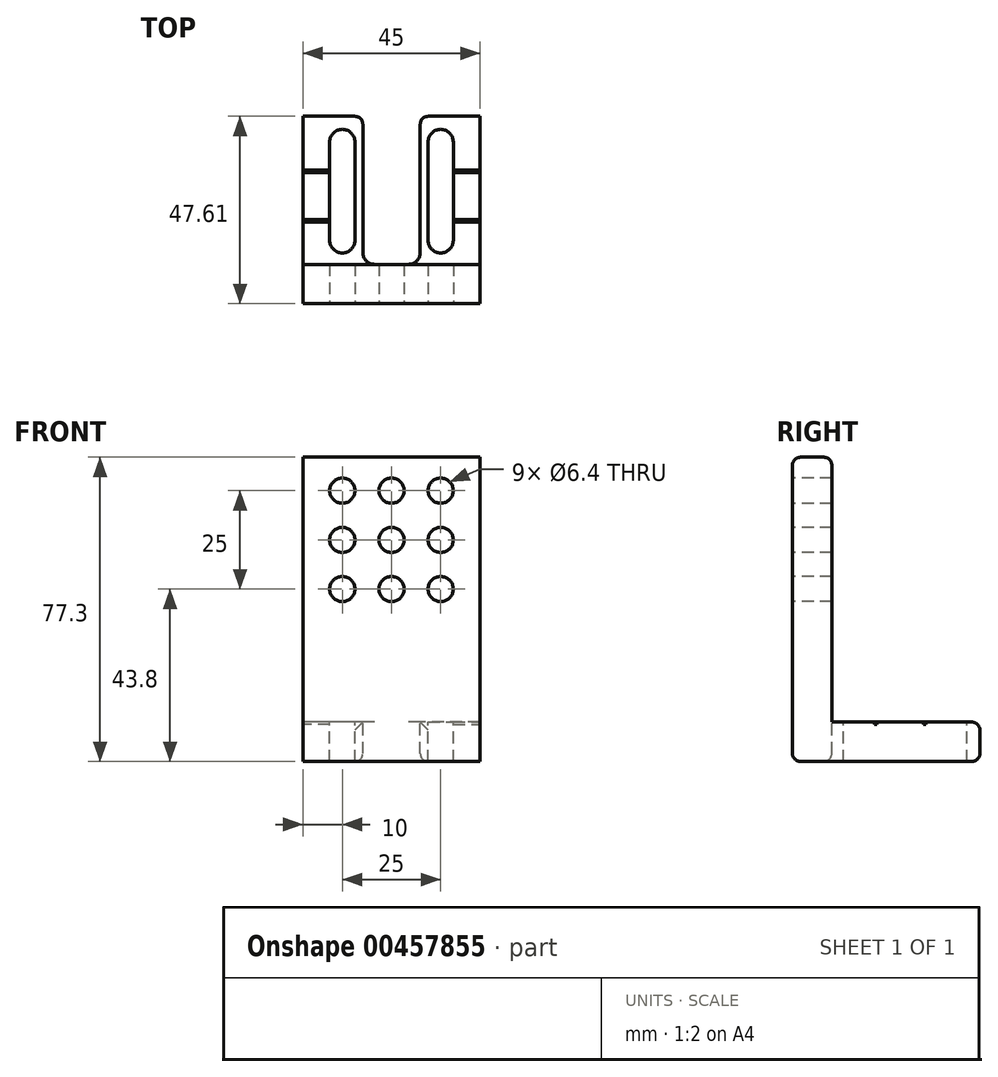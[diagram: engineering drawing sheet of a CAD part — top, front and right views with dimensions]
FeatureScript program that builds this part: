
annotation { "Feature Type Name" : "Feature", "Feature Type Description" : "" }
export const myFeature = defineFeature(function(context is Context, id is Id, definition is map)
    precondition{}
    {
        {
            var Q0;
            Q0=qCreatedBy(makeId("Right.planeOp"),FACE);
            var sketch = newSketch(context, id + "F0", { "sketchPlane" : qUnion([Q0])});
            skLineSegment(sketch, "E0", {"start": v(0, 0) * mm, "end": v(0, 67.3) * mm});
            skLineSegment(sketch, "E1", {"start": v(0, 67.3) * mm, "end": v(-10, 67.3) * mm});
            skLineSegment(sketch, "E2", {"start": v(-10, 67.3) * mm, "end": v(-10, -10) * mm});
            skLineSegment(sketch, "E3", {"start": v(-10, -10) * mm, "end": v(37.61, -10) * mm});
            skLineSegment(sketch, "E4", {"start": v(37.61, -10) * mm, "end": v(37.61, 0) * mm});
            skLineSegment(sketch, "E5", {"start": v(37.61, 0) * mm, "end": v(0, 0) * mm});
            skLineSegment(sketch, "E6", {"start": v(-10, 46.3) * mm, "end": v(0, 46.3) * mm, "construction": true});
            skLineSegment(sketch, "E7", {"start": v(23.61, 0) * mm, "end": v(23.61, -10) * mm, "construction": true});
            skLineSegment(sketch, "E8", {"start": v(11.11, 0) * mm, "end": v(11.11, -10) * mm, "construction": true});
            skLineSegment(sketch, "E9", {"start": v(6, 0) * mm, "end": v(6, -10) * mm, "construction": true});
            skPoint(sketch, "E9.endSnap0", {"position": v(13.8, -10) * mm});
            skSolve(sketch);
        }
        {
            var Q0;
            Q0=makeQuery(id+"F0.imprint","IMPRINT",FACE,{"disambiguationData":[TD([[makeQuery(id+"F0.imprint","IMPRINT",EDGE,{"derivedFrom":sQuery(id+"F0.wireOp",EDGE,"E0")}),1.0]])]});
            extrude(context, id + "F1", {"entities" : qUnion([Q0]), "depth" : 45 * mm});
        }
        {
            var Q0;
            Q0=makeQuery(id+"F1.opExtrude","SWEPT_FACE",FACE,{"disambiguationData":[OSD([sQuery(id+"F0.wireOp",EDGE,"E5")])]});
            var sketch = newSketch(context, id + "F2", { "sketchPlane" : qUnion([Q0])});
            skLineSegment(sketch, "E10", {"start": v(22.5, 37.61) * mm, "end": v(22.5, 0) * mm, "construction": true});
            skPoint(sketch, "E11.0", {"position": v(0, 23.61) * mm});
            skPoint(sketch, "E12.0", {"position": v(0, 11.11) * mm});
            skCircle(sketch, "E13", {"center": v(10, 23.61) * mm, "radius": 3.2 * mm, "construction": true});
            skCircle(sketch, "E14", {"center": v(10, 11.11) * mm, "radius": 3.2 * mm, "construction": true});
            skCircle(sketch, "E15", {"center": v(35, 11.11) * mm, "radius": 3.2 * mm, "construction": true});
            skCircle(sketch, "E16", {"center": v(35, 23.61) * mm, "radius": 3.2 * mm, "construction": true});
            skArc(sketch, "E17", {"start": v(13.2, 31.11) * mm, "mid": v(10, 34.31) * mm, "end": v(6.8, 31.11) * mm});
            skArc(sketch, "E18", {"start": v(38.2, 31.11) * mm, "mid": v(35, 34.31) * mm, "end": v(31.8, 31.11) * mm});
            skArc(sketch, "E19", {"start": v(6.8, 6.11) * mm, "mid": v(10, 2.91) * mm, "end": v(13.2, 6.11) * mm});
            skArc(sketch, "E20", {"start": v(31.8, 6.11) * mm, "mid": v(35, 2.91) * mm, "end": v(38.2, 6.11) * mm});
            skLineSegment(sketch, "E21", {"start": v(6.8, 31.11) * mm, "end": v(6.8, 6.11) * mm});
            skLineSegment(sketch, "E22", {"start": v(13.2, 31.11) * mm, "end": v(13.2, 6.11) * mm});
            skLineSegment(sketch, "E23", {"start": v(31.8, 31.11) * mm, "end": v(31.8, 6.11) * mm});
            skLineSegment(sketch, "E24", {"start": v(38.2, 6.11) * mm, "end": v(38.2, 31.11) * mm});
            skLineSegment(sketch, "E25.bottom", {"start": v(15.2, 37.61) * mm, "end": v(29.8, 37.61) * mm});
            skLineSegment(sketch, "E25.top", {"start": v(15.2, 0) * mm, "end": v(29.8, 0) * mm});
            skLineSegment(sketch, "E25.left", {"start": v(15.2, 37.61) * mm, "end": v(15.2, 0) * mm});
            skLineSegment(sketch, "E25.right", {"start": v(29.8, 37.61) * mm, "end": v(29.8, 0) * mm});
            skLineSegment(sketch, "E26.bottom", {"start": v(6.8, 10.81) * mm, "end": v(0, 10.81) * mm});
            skLineSegment(sketch, "E26.top", {"start": v(6.8, 11.41) * mm, "end": v(0, 11.41) * mm});
            skLineSegment(sketch, "E26.left", {"start": v(6.8, 10.81) * mm, "end": v(6.8, 11.41) * mm});
            skLineSegment(sketch, "E26.right", {"start": v(0, 10.81) * mm, "end": v(0, 11.41) * mm});
            skLineSegment(sketch, "E27.bottom", {"start": v(6.8, 23.31) * mm, "end": v(0, 23.31) * mm});
            skLineSegment(sketch, "E27.top", {"start": v(6.8, 23.91) * mm, "end": v(0, 23.91) * mm});
            skLineSegment(sketch, "E27.left", {"start": v(6.8, 23.31) * mm, "end": v(6.8, 23.91) * mm});
            skLineSegment(sketch, "E27.right", {"start": v(0, 23.31) * mm, "end": v(0, 23.91) * mm});
            skLineSegment(sketch, "E28.bottom", {"start": v(38.2, 10.81) * mm, "end": v(45, 10.81) * mm});
            skLineSegment(sketch, "E28.top", {"start": v(38.2, 11.41) * mm, "end": v(45, 11.41) * mm});
            skLineSegment(sketch, "E28.left", {"start": v(38.2, 10.81) * mm, "end": v(38.2, 11.41) * mm});
            skLineSegment(sketch, "E28.right", {"start": v(45, 10.81) * mm, "end": v(45, 11.41) * mm});
            skLineSegment(sketch, "E29.bottom", {"start": v(38.2, 23.31) * mm, "end": v(45, 23.31) * mm});
            skLineSegment(sketch, "E29.top", {"start": v(38.2, 23.91) * mm, "end": v(45, 23.91) * mm});
            skLineSegment(sketch, "E29.left", {"start": v(38.2, 23.31) * mm, "end": v(38.2, 23.91) * mm});
            skLineSegment(sketch, "E29.right", {"start": v(45, 23.31) * mm, "end": v(45, 23.91) * mm});
            skSolve(sketch);
        }
        {
            var Q0;
            Q0=makeQuery(id+"F2.imprint","IMPRINT",FACE,{"disambiguationData":[TD([[makeQuery(id+"F2.imprint","IMPRINT",EDGE,{"derivedFrom":sQuery(id+"F2.wireOp",EDGE,"E17")}),1.0]])]});
            var Q1;
            Q1=makeQuery(id+"F2.imprint","IMPRINT",FACE,{"disambiguationData":[TD([[makeQuery(id+"F2.imprint","IMPRINT",EDGE,{"derivedFrom":sQuery(id+"F2.wireOp",EDGE,"o95GAQiW-py6V-pouL-C4bO-UlPNCyXJZhJI")}),1.0]])]});
            var Q2;
            Q2=makeQuery(id+"F2.imprint","IMPRINT",FACE,{"disambiguationData":[TD([[makeQuery(id+"F2.imprint","IMPRINT",EDGE,{"derivedFrom":sQuery(id+"F2.wireOp",EDGE,"E18")}),1.0]])]});
            extrude(context, id + "F3", {"entities" : qUnion([Q0, Q1, Q2]), "operationType" : NewBodyOperationType.REMOVE, "oppositeDirection" : true, "depth" : 10 * mm});
        }
        {
            var Q0;
            Q0=makeQuery(id+"F1.opExtrude","SWEPT_EDGE",EDGE,{"disambiguationData":[OSD([sQuery(id+"F0.wireOp",EDGE,"E3"),sQuery(id+"F0.wireOp",EDGE,"E4")])]});
            var Q1;
            Q1=makeQuery(id+"F1.opExtrude","SWEPT_EDGE",EDGE,{"disambiguationData":[OSD([sQuery(id+"F0.wireOp",EDGE,"E2"),sQuery(id+"F0.wireOp",EDGE,"E3")])]});
            var Q2;
            Q2=makeQuery(id+"F1.opExtrude","SWEPT_EDGE",EDGE,{"disambiguationData":[OSD([sQuery(id+"F0.wireOp",EDGE,"E0"),sQuery(id+"F0.wireOp",EDGE,"E1")])]});
            var Q3;
            Q3=makeQuery(id+"F1.opExtrude","SWEPT_EDGE",EDGE,{"disambiguationData":[OSD([sQuery(id+"F0.wireOp",EDGE,"E1"),sQuery(id+"F0.wireOp",EDGE,"E2")])]});
            fillet(context, id + "F4", {"entities" : qUnion([Q0, Q1, Q2, Q3]), "radius" : 2 * mm, "tangentPropagation" : true, "allowEdgeOverflow" : false});
        }
        {
            var Q0;
            Q0=makeQuery(id+"F1.opExtrude","SWEPT_FACE",FACE,{"disambiguationData":[OSD([sQuery(id+"F0.wireOp",EDGE,"E2")])]});
            var sketch = newSketch(context, id + "F5", { "sketchPlane" : qUnion([Q0])});
            skPoint(sketch, "E30.0", {"position": v(0, 46.3) * mm});
            skCircle(sketch, "E31", {"center": v(22.5, 46.3) * mm, "radius": 3.2 * mm});
            skPoint(sketch, "E31.centerSnap0", {"position": v(22.5, 65.3) * mm});
            skCircle(sketch, "E32", {"center": v(22.5, 58.8) * mm, "radius": 3.2 * mm});
            skCircle(sketch, "E33", {"center": v(22.5, 33.8) * mm, "radius": 3.2 * mm});
            skCircle(sketch, "E34", {"center": v(35, 46.3) * mm, "radius": 3.2 * mm});
            skCircle(sketch, "E35", {"center": v(35, 58.8) * mm, "radius": 3.2 * mm});
            skCircle(sketch, "E36", {"center": v(35, 33.8) * mm, "radius": 3.2 * mm});
            skCircle(sketch, "E37", {"center": v(10, 58.8) * mm, "radius": 3.2 * mm});
            skCircle(sketch, "E38", {"center": v(10, 46.3) * mm, "radius": 3.2 * mm});
            skCircle(sketch, "E39", {"center": v(10, 33.8) * mm, "radius": 3.2 * mm});
            skSolve(sketch);
        }
        {
            var Q0;
            Q0=makeQuery(id+"F5.imprint","IMPRINT",FACE,{"disambiguationData":[TD([[makeQuery(id+"F5.imprint","IMPRINT",EDGE,{"derivedFrom":sQuery(id+"F5.wireOp",EDGE,"E37")}),1.0]])]});
            var Q1;
            Q1=makeQuery(id+"F5.imprint","IMPRINT",FACE,{"disambiguationData":[TD([[makeQuery(id+"F5.imprint","IMPRINT",EDGE,{"derivedFrom":sQuery(id+"F5.wireOp",EDGE,"E32")}),1.0]])]});
            var Q2;
            Q2=makeQuery(id+"F5.imprint","IMPRINT",FACE,{"disambiguationData":[TD([[makeQuery(id+"F5.imprint","IMPRINT",EDGE,{"derivedFrom":sQuery(id+"F5.wireOp",EDGE,"E35")}),1.0]])]});
            var Q3;
            Q3=makeQuery(id+"F5.imprint","IMPRINT",FACE,{"disambiguationData":[TD([[makeQuery(id+"F5.imprint","IMPRINT",EDGE,{"derivedFrom":sQuery(id+"F5.wireOp",EDGE,"E34")}),1.0]])]});
            var Q4;
            Q4=makeQuery(id+"F5.imprint","IMPRINT",FACE,{"disambiguationData":[TD([[makeQuery(id+"F5.imprint","IMPRINT",EDGE,{"derivedFrom":sQuery(id+"F5.wireOp",EDGE,"E31")}),1.0]])]});
            var Q5;
            Q5=makeQuery(id+"F5.imprint","IMPRINT",FACE,{"disambiguationData":[TD([[makeQuery(id+"F5.imprint","IMPRINT",EDGE,{"derivedFrom":sQuery(id+"F5.wireOp",EDGE,"E38")}),1.0]])]});
            var Q6;
            Q6=makeQuery(id+"F5.imprint","IMPRINT",FACE,{"disambiguationData":[TD([[makeQuery(id+"F5.imprint","IMPRINT",EDGE,{"derivedFrom":sQuery(id+"F5.wireOp",EDGE,"E39")}),1.0]])]});
            var Q7;
            Q7=makeQuery(id+"F5.imprint","IMPRINT",FACE,{"disambiguationData":[TD([[makeQuery(id+"F5.imprint","IMPRINT",EDGE,{"derivedFrom":sQuery(id+"F5.wireOp",EDGE,"E33")}),1.0]])]});
            var Q8;
            Q8=makeQuery(id+"F5.imprint","IMPRINT",FACE,{"disambiguationData":[TD([[makeQuery(id+"F5.imprint","IMPRINT",EDGE,{"derivedFrom":sQuery(id+"F5.wireOp",EDGE,"E36")}),1.0]])]});
            extrude(context, id + "F6", {"entities" : qUnion([Q0, Q1, Q2, Q3, Q4, Q5, Q6, Q7, Q8]), "operationType" : NewBodyOperationType.REMOVE, "oppositeDirection" : true, "depth" : 10 * mm});
        }
        {
            var Q0;
            Q0=makeQuery(id+"F2.imprint","IMPRINT",FACE,{"disambiguationData":[TD([[makeQuery(id+"F2.imprint","IMPRINT",EDGE,{"derivedFrom":sQuery(id+"F2.wireOp",EDGE,"E25.bottom")}),1.0]])]});
            extrude(context, id + "F7", {"entities" : qUnion([Q0]), "operationType" : NewBodyOperationType.REMOVE, "oppositeDirection" : true, "depth" : 10 * mm});
        }
        {
            var Q0;
            Q0=makeQuery(id+"F7.boolean.opBoolean","COPY",EDGE,{"derivedFrom":makeQuery(id+"F7.opExtrude","SWEPT_EDGE",EDGE,{"disambiguationData":[OSD([sQuery(id+"F0.wireOp",EDGE,"E0"),sQuery(id+"F0.wireOp",EDGE,"E5"),sQuery(id+"F2.wireOp",EDGE,"E25.top"),sQuery(id+"F2.wireOp",EDGE,"E25.right")])]})});
            var Q1;
            Q1=makeQuery(id+"F7.boolean.opBoolean","COPY",EDGE,{"derivedFrom":makeQuery(id+"F7.opExtrude","SWEPT_EDGE",EDGE,{"disambiguationData":[OSD([sQuery(id+"F0.wireOp",EDGE,"E0"),sQuery(id+"F0.wireOp",EDGE,"E5"),sQuery(id+"F2.wireOp",EDGE,"E25.top"),sQuery(id+"F2.wireOp",EDGE,"E25.left")])]})});
            fillet(context, id + "F8", {"entities" : qUnion([Q0, Q1]), "radius" : 3 * mm, "tangentPropagation" : true, "allowEdgeOverflow" : false});
        }
        {
            var Q0;
            Q0=makeQuery(id+"F7.boolean.opBoolean","COPY",EDGE,{"derivedFrom":makeQuery(id+"F7.opExtrude","SWEPT_EDGE",EDGE,{"disambiguationData":[OSD([sQuery(id+"F0.wireOp",EDGE,"E4"),sQuery(id+"F0.wireOp",EDGE,"E5"),sQuery(id+"F2.wireOp",EDGE,"E25.bottom"),sQuery(id+"F2.wireOp",EDGE,"E25.left")])]})});
            var Q1;
            Q1=makeQuery(id+"F7.boolean.opBoolean","INTERSECT",EDGE,{"derivedFrom":[makeQuery(id+"F4.opFillet","BLEND_FACE",FACE,{"disambiguationData":[OSD([sQuery(id+"F0.wireOp",EDGE,"E3"),sQuery(id+"F0.wireOp",EDGE,"E4")])]}),makeQuery(id+"F7.opExtrude","SWEPT_FACE",FACE,{"disambiguationData":[OSD([sQuery(id+"F2.wireOp",EDGE,"E25.left")])]})]});
            var Q2;
            {var subQ0=sQuery(id+"F0.wireOp",EDGE,"E5");var subQ1=sQuery(id+"F0.wireOp",EDGE,"E4");Q2=makeQuery(id+"F7.boolean.opBoolean","SPLIT",EDGE,{"disambiguationData":[TD([makeQuery(id+"F7.opExtrude","SWEPT_FACE",FACE,{"disambiguationData":[OSD([sQuery(id+"F2.wireOp",EDGE,"E25.right")])]})])],"derivedFrom":makeQuery(id+"F1.opExtrude","SWEPT_EDGE",EDGE,{"disambiguationData":[OSD([subQ1,subQ0])]})});}
            var Q3;
            {var subQ0=sQuery(id+"F0.wireOp",EDGE,"E5");var subQ1=sQuery(id+"F0.wireOp",EDGE,"E4");Q3=makeQuery(id+"F7.boolean.opBoolean","SPLIT",EDGE,{"disambiguationData":[TD([makeQuery(id+"F7.opExtrude","SWEPT_FACE",FACE,{"disambiguationData":[OSD([sQuery(id+"F2.wireOp",EDGE,"E25.left")])]})])],"derivedFrom":makeQuery(id+"F1.opExtrude","SWEPT_EDGE",EDGE,{"disambiguationData":[OSD([subQ1,subQ0])]})});}
            fillet(context, id + "F9", {"entities" : qUnion([Q0, Q1, Q2, Q3]), "radius" : 2 * mm, "tangentPropagation" : true, "allowEdgeOverflow" : false});
        }
        {
            var Q0;
            Q0=makeQuery(id+"F2.imprint","IMPRINT",FACE,{"disambiguationData":[TD([[makeQuery(id+"F2.imprint","IMPRINT",EDGE,{"derivedFrom":sQuery(id+"F2.wireOp",EDGE,"E26.bottom")}),-1.0]])]});
            var Q1;
            Q1=makeQuery(id+"F2.imprint","IMPRINT",FACE,{"disambiguationData":[TD([[makeQuery(id+"F2.imprint","IMPRINT",EDGE,{"derivedFrom":sQuery(id+"F2.wireOp",EDGE,"E27.bottom")}),-1.0]])]});
            var Q2;
            Q2=makeQuery(id+"F2.imprint","IMPRINT",FACE,{"disambiguationData":[TD([[makeQuery(id+"F2.imprint","IMPRINT",EDGE,{"derivedFrom":sQuery(id+"F2.wireOp",EDGE,"E28.bottom")}),1.0]])]});
            var Q3;
            Q3=makeQuery(id+"F2.imprint","IMPRINT",FACE,{"disambiguationData":[TD([[makeQuery(id+"F2.imprint","IMPRINT",EDGE,{"derivedFrom":sQuery(id+"F2.wireOp",EDGE,"E29.bottom")}),1.0]])]});
            extrude(context, id + "F10", {"entities" : qUnion([Q0, Q1, Q2, Q3]), "operationType" : NewBodyOperationType.REMOVE, "oppositeDirection" : true, "depth" : 0.6 * mm});
        }
    });
